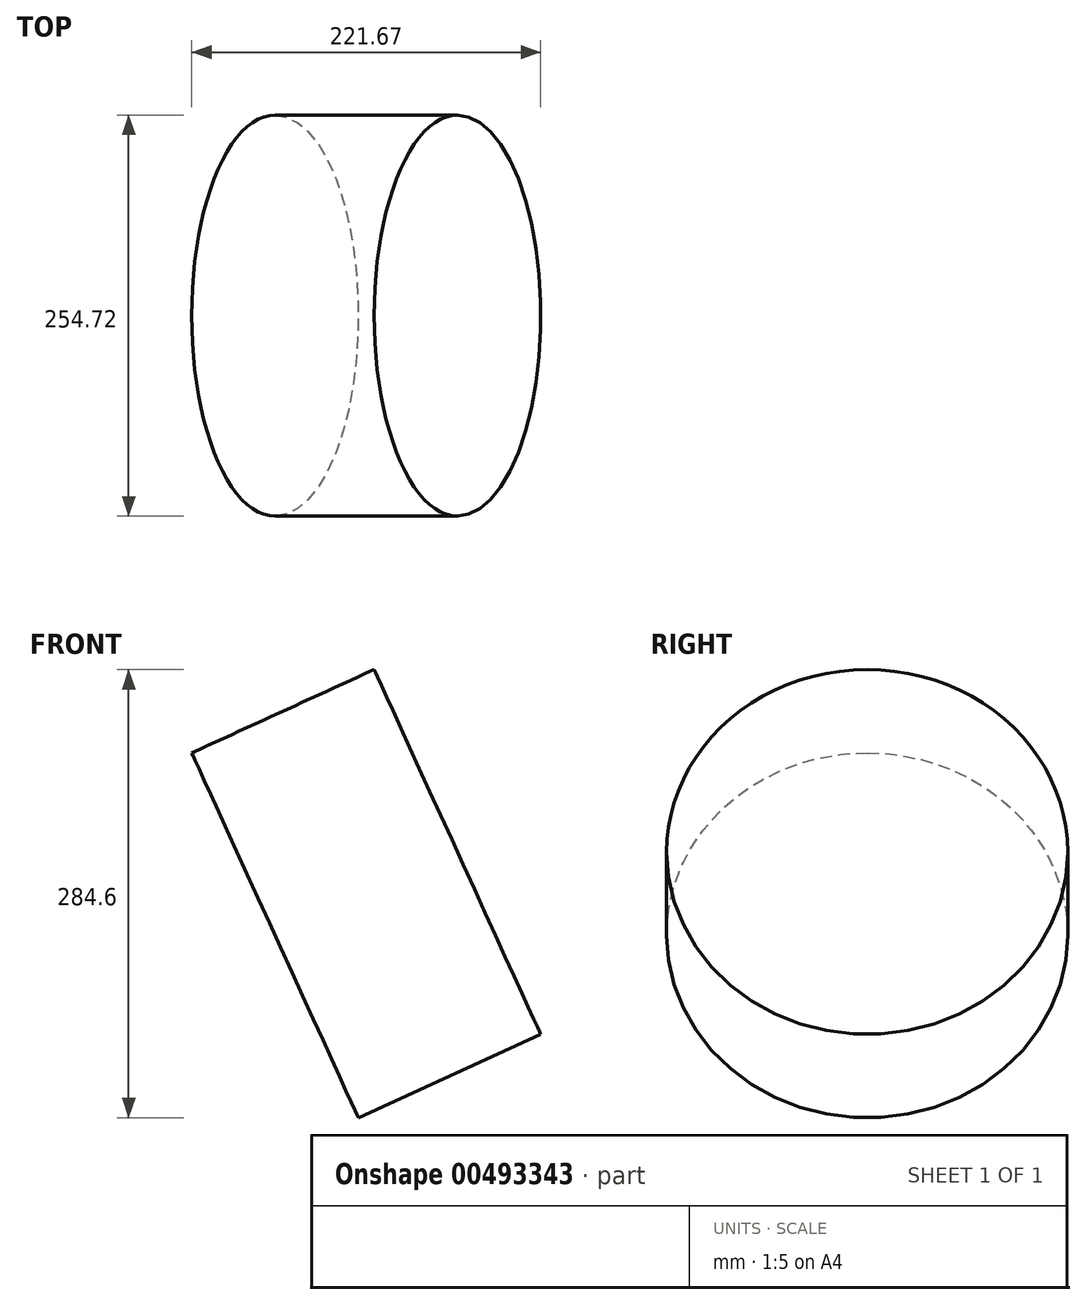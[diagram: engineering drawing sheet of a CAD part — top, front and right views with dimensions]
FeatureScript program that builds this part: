
annotation { "Feature Type Name" : "Feature", "Feature Type Description" : "" }
export const myFeature = defineFeature(function(context is Context, id is Id, definition is map)
    precondition{}
    {
        {
            var Q0;
            Q0=qCreatedBy(makeId("Front.planeOp"),FACE);
            var sketch = newSketch(context, id + "F0", { "sketchPlane" : qUnion([Q0])});
            skCircle(sketch, "E0.cCircle", {"center": v(0, 0) * mm, "radius": 90.06 * mm, "construction": true});
            skLineSegment(sketch, "E0.0", {"start": v(-84.38, 31.47) * mm, "end": v(31.47, 84.38) * mm});
            skLineSegment(sketch, "E0.1", {"start": v(31.47, 84.38) * mm, "end": v(84.38, -31.47) * mm});
            skLineSegment(sketch, "E0.2", {"start": v(84.38, -31.47) * mm, "end": v(-31.47, -84.38) * mm});
            skLineSegment(sketch, "E0.3", {"start": v(-31.47, -84.38) * mm, "end": v(-84.38, 31.47) * mm});
            skSolve(sketch);
        }
        {
            var Q0;
            Q0=makeQuery(id+"F0.imprint","IMPRINT",FACE,{"disambiguationData":[TD([[makeQuery(id+"F0.imprint","IMPRINT",EDGE,{"derivedFrom":sQuery(id+"F0.wireOp",EDGE,"E0.0")}),-1.0]])]});
            var Q1;
            Q1=sQuery(id+"F0.wireOp",EDGE,"E0.0");
            revolve(context, id + "F1", {"entities" : qUnion([Q0]), "axis" : qUnion([Q1]), "revolveType" : RevolveType.FULL});
        }
    });
